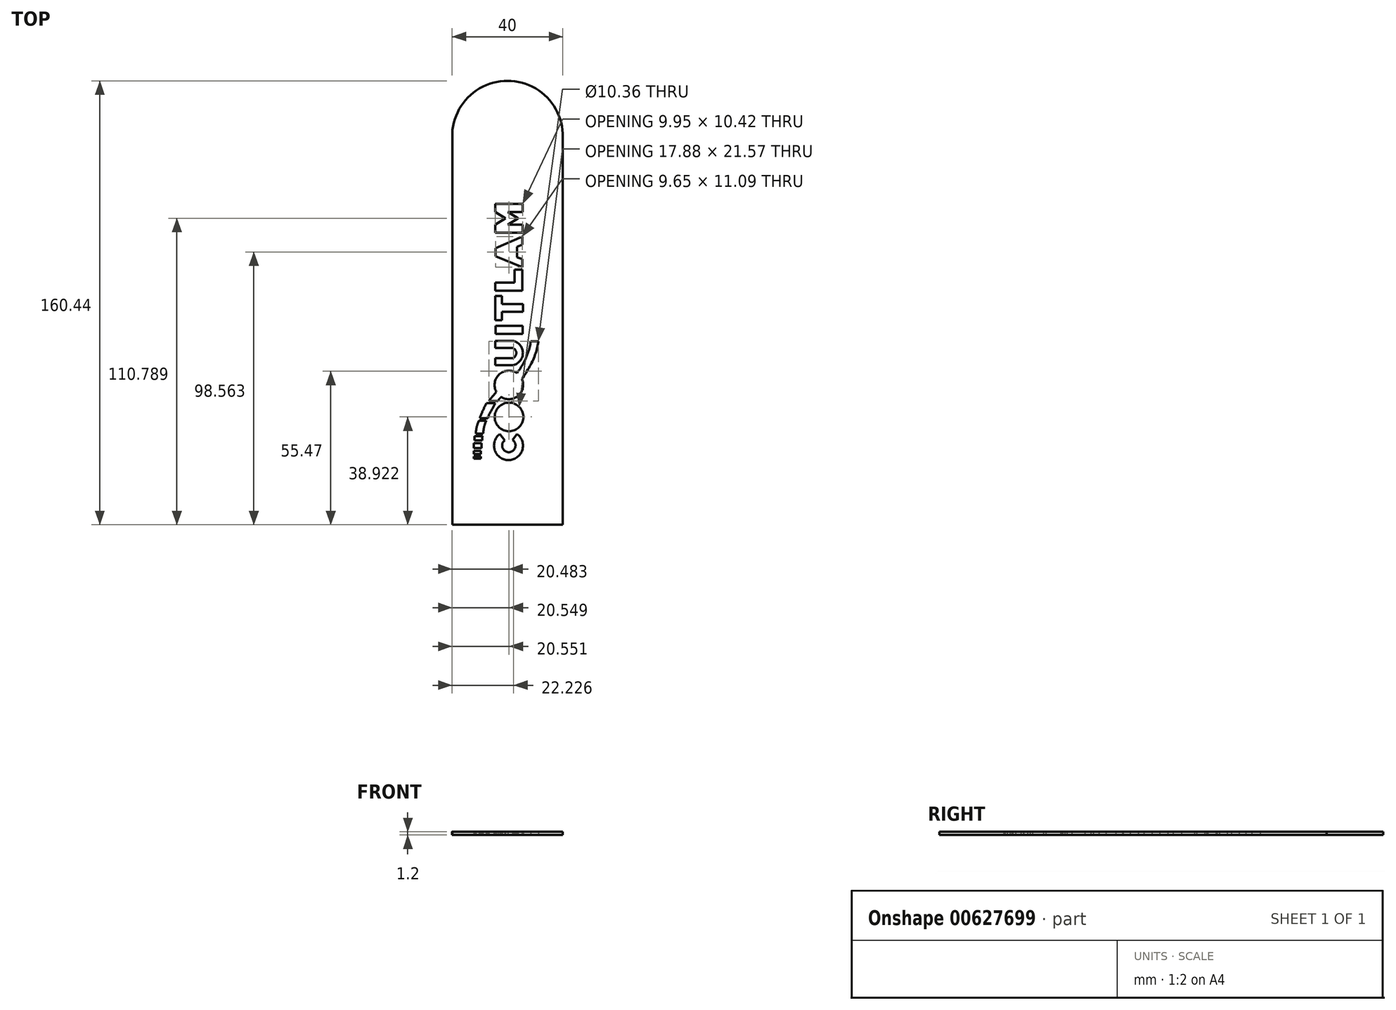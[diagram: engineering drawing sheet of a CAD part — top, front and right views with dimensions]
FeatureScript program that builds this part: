
annotation { "Feature Type Name" : "Feature", "Feature Type Description" : "" }
export const myFeature = defineFeature(function(context is Context, id is Id, definition is map)
    precondition{}
    {
        {
            var Q0;
            Q0=qCreatedBy(makeId("Top.planeOp"),FACE);
            var sketch = newSketch(context, id + "F0", { "sketchPlane" : qUnion([Q0])});
            skArc(sketch, "E0", {"start": v(-6.3, 54.09) * mm, "mid": v(-26.29, 74.53) * mm, "end": v(-46.28, 54.09) * mm});
            skLineSegment(sketch, "E1", {"start": v(-46.28, 54.09) * mm, "end": v(-46.28, -85.91) * mm});
            skLineSegment(sketch, "E2", {"start": v(-6.3, 54.09) * mm, "end": v(-6.3, -85.91) * mm});
            skLineSegment(sketch, "E3", {"start": v(-46.28, -85.91) * mm, "end": v(-6.3, -85.91) * mm});
            skArc(sketch, "E4", {"start": v(-27.3, -55.41) * mm, "mid": v(-25.75, -59.72) * mm, "end": v(-24.44, -55.33) * mm});
            skArc(sketch, "E5", {"start": v(-29.02, -53.12) * mm, "mid": v(-25.94, -62.57) * mm, "end": v(-22.87, -53.12) * mm});
            skLineSegment(sketch, "E6", {"start": v(-29.02, -53.12) * mm, "end": v(-27.3, -55.41) * mm});
            skLineSegment(sketch, "E7", {"start": v(-24.44, -55.33) * mm, "end": v(-22.87, -53.12) * mm});
            skCircle(sketch, "E8", {"center": v(-25.74, -46.99) * mm, "radius": 2.44 * mm});
            skCircle(sketch, "E9", {"center": v(-25.74, -46.99) * mm, "radius": 5.18 * mm});
            skLineSegment(sketch, "E10", {"start": v(-30.76, 1.6) * mm, "end": v(-30.76, -1.39) * mm});
            skLineSegment(sketch, "E11", {"start": v(-30.76, -1.39) * mm, "end": v(-20.98, -1.39) * mm});
            skLineSegment(sketch, "E12", {"start": v(-20.98, -1.39) * mm, "end": v(-20.98, 6.3) * mm});
            skLineSegment(sketch, "E13", {"start": v(-20.98, 6.3) * mm, "end": v(-23.72, 6.3) * mm});
            skLineSegment(sketch, "E14", {"start": v(-23.72, 6.3) * mm, "end": v(-23.72, 1.6) * mm});
            skLineSegment(sketch, "E15", {"start": v(-23.72, 1.6) * mm, "end": v(-30.76, 1.6) * mm});
            skLineSegment(sketch, "E16", {"start": v(-30.68, -3.24) * mm, "end": v(-30.68, -12) * mm});
            skLineSegment(sketch, "E17", {"start": v(-30.68, -12) * mm, "end": v(-28.35, -12) * mm});
            skLineSegment(sketch, "E18", {"start": v(-28.35, -12) * mm, "end": v(-28.35, -8.95) * mm});
            skLineSegment(sketch, "E19", {"start": v(-28.35, -8.95) * mm, "end": v(-20.76, -8.95) * mm});
            skLineSegment(sketch, "E20", {"start": v(-20.76, -8.95) * mm, "end": v(-20.76, -6.2) * mm});
            skLineSegment(sketch, "E21", {"start": v(-20.76, -6.2) * mm, "end": v(-28.35, -6.2) * mm});
            skLineSegment(sketch, "E22", {"start": v(-28.35, -6.2) * mm, "end": v(-28.35, -3.24) * mm});
            skLineSegment(sketch, "E23", {"start": v(-28.35, -3.24) * mm, "end": v(-30.68, -3.24) * mm});
            skArc(sketch, "E24", {"start": v(-24.25, -25.67) * mm, "mid": v(-23.12, -23.78) * mm, "end": v(-24.46, -22.03) * mm});
            skArc(sketch, "E25", {"start": v(-24.25, -28.22) * mm, "mid": v(-20.74, -23.75) * mm, "end": v(-24.46, -19.45) * mm});
            skLineSegment(sketch, "E26", {"start": v(-24.46, -19.45) * mm, "end": v(-30.73, -19.45) * mm});
            skLineSegment(sketch, "E27", {"start": v(-30.73, -19.45) * mm, "end": v(-30.73, -22.03) * mm});
            skLineSegment(sketch, "E28", {"start": v(-30.73, -22.03) * mm, "end": v(-24.46, -22.03) * mm});
            skLineSegment(sketch, "E29", {"start": v(-24.25, -25.67) * mm, "end": v(-30.73, -25.67) * mm});
            skLineSegment(sketch, "E30", {"start": v(-30.73, -25.67) * mm, "end": v(-30.73, -28.22) * mm});
            skLineSegment(sketch, "E31", {"start": v(-30.73, -28.22) * mm, "end": v(-24.25, -28.22) * mm});
            skLineSegment(sketch, "E32", {"start": v(-30.63, -13.98) * mm, "end": v(-30.63, -16.92) * mm});
            skLineSegment(sketch, "E33", {"start": v(-30.63, -16.92) * mm, "end": v(-20.8, -16.92) * mm});
            skLineSegment(sketch, "E34", {"start": v(-20.8, -16.92) * mm, "end": v(-20.8, -13.98) * mm});
            skLineSegment(sketch, "E35", {"start": v(-20.8, -13.98) * mm, "end": v(-30.63, -13.98) * mm});
            skLineSegment(sketch, "E36", {"start": v(-24.85, 13.76) * mm, "end": v(-24.85, 11.53) * mm});
            skLineSegment(sketch, "E37", {"start": v(-24.85, 11.53) * mm, "end": v(-27.5, 12.61) * mm});
            skLineSegment(sketch, "E38", {"start": v(-27.5, 12.61) * mm, "end": v(-24.85, 13.76) * mm});
            skLineSegment(sketch, "E39", {"start": v(-20.98, 18.2) * mm, "end": v(-30.63, 14.04) * mm});
            skLineSegment(sketch, "E40", {"start": v(-30.63, 14.04) * mm, "end": v(-30.63, 11.12) * mm});
            skLineSegment(sketch, "E41", {"start": v(-30.63, 11.12) * mm, "end": v(-20.98, 7.1) * mm});
            skLineSegment(sketch, "E42", {"start": v(-20.98, 7.1) * mm, "end": v(-20.98, 10.1) * mm});
            skLineSegment(sketch, "E43", {"start": v(-20.98, 10.1) * mm, "end": v(-22.8, 10.69) * mm});
            skLineSegment(sketch, "E44", {"start": v(-22.8, 10.69) * mm, "end": v(-22.8, 14.54) * mm});
            skLineSegment(sketch, "E45", {"start": v(-22.8, 14.54) * mm, "end": v(-20.98, 15.32) * mm});
            skLineSegment(sketch, "E46", {"start": v(-20.98, 15.32) * mm, "end": v(-20.98, 18.2) * mm});
            skLineSegment(sketch, "E47", {"start": v(-20.76, 19.67) * mm, "end": v(-30.72, 19.67) * mm});
            skLineSegment(sketch, "E48", {"start": v(-30.72, 19.67) * mm, "end": v(-30.72, 22.5) * mm});
            skLineSegment(sketch, "E49", {"start": v(-30.72, 22.5) * mm, "end": v(-27.1, 24.83) * mm});
            skLineSegment(sketch, "E50", {"start": v(-27.1, 24.83) * mm, "end": v(-30.72, 27.05) * mm});
            skLineSegment(sketch, "E51", {"start": v(-30.72, 27.05) * mm, "end": v(-30.72, 30.09) * mm});
            skLineSegment(sketch, "E52", {"start": v(-30.72, 30.09) * mm, "end": v(-20.76, 30.09) * mm});
            skLineSegment(sketch, "E53", {"start": v(-20.76, 30.09) * mm, "end": v(-20.76, 27.05) * mm});
            skLineSegment(sketch, "E54", {"start": v(-20.76, 27.05) * mm, "end": v(-26.15, 27.05) * mm});
            skLineSegment(sketch, "E55", {"start": v(-26.15, 27.05) * mm, "end": v(-22.52, 24.83) * mm});
            skLineSegment(sketch, "E56", {"start": v(-22.52, 24.83) * mm, "end": v(-26.15, 22.5) * mm});
            skLineSegment(sketch, "E57", {"start": v(-26.15, 22.5) * mm, "end": v(-20.76, 22.5) * mm});
            skLineSegment(sketch, "E58", {"start": v(-20.76, 22.5) * mm, "end": v(-20.76, 19.67) * mm});
            skLineSegment(sketch, "E59", {"start": v(-37.74, -53.07) * mm, "end": v(-35.16, -53.07) * mm});
            skLineSegment(sketch, "E60", {"start": v(-36.62, -48.28) * mm, "end": v(-33.96, -48.28) * mm});
            skFitSpline(sketch, "E61", {"points": [v(-33.96, -48.28) * mm, v(-35.16, -53.07) * mm], "startDerivative": vector(-2.34, -4.67) * mm, "endDerivative": vector(-0.73, -4.9) * mm});
            skLineSegment(sketch, "E62", {"start": v(-33.9, -42.04) * mm, "end": v(-30.66, -42.04) * mm});
            skLineSegment(sketch, "E63.bottom", {"start": v(-36.28, -47.39) * mm, "end": v(-33.39, -47.39) * mm});
            skLineSegment(sketch, "E63.top", {"start": v(-36.28, -47.39) * mm, "end": v(-33.39, -47.39) * mm});
            skLineSegment(sketch, "E63.left", {"start": v(-36.28, -47.39) * mm, "end": v(-36.28, -47.39) * mm});
            skLineSegment(sketch, "E63.right", {"start": v(-33.39, -47.39) * mm, "end": v(-33.39, -47.39) * mm});
            skFitSpline(sketch, "E64", {"points": [v(-33.9, -42.04) * mm, v(-36.28, -47.39) * mm], "startDerivative": vector(-2.85, -5.33) * mm, "endDerivative": vector(-1.75, -5.33) * mm});
            skFitSpline(sketch, "E65", {"points": [v(-30.66, -42.04) * mm, v(-33.39, -47.39) * mm], "startDerivative": vector(-3.36, -5.84) * mm, "endDerivative": vector(-1.75, -5.62) * mm});
            skLineSegment(sketch, "E66", {"start": v(-17.88, -19.65) * mm, "end": v(-15.13, -19.65) * mm});
            skFitSpline(sketch, "E67", {"points": [v(-15.13, -19.65) * mm, v(-21.13, -33.23) * mm], "startDerivative": vector(-1.76, -13.9) * mm, "endDerivative": vector(-9.3, -12.6) * mm});
            skFitSpline(sketch, "E68", {"points": [v(-17.88, -19.65) * mm, v(-22.88, -31.16) * mm], "startDerivative": vector(-1.76, -12.35) * mm, "endDerivative": vector(-7.81, -10.68) * mm});
            skCircle(sketch, "E69", {"center": v(-25.81, -35.4) * mm, "radius": 5.16 * mm});
            skLineSegment(sketch, "E70", {"start": v(-33, -41.23) * mm, "end": v(-29.76, -41.23) * mm});
            skFitSpline(sketch, "E71", {"points": [v(-30.31, -37.93) * mm, v(-33, -41.23) * mm], "startDerivative": vector(-3.27, -3.7) * mm, "endDerivative": vector(-1.73, -2.89) * mm});
            skFitSpline(sketch, "E72", {"points": [v(-28.57, -39.77) * mm, v(-29.76, -41.23) * mm], "startDerivative": vector(-1.34, -1.28) * mm, "endDerivative": vector(-0.7, -1.8) * mm});
            skArc(sketch, "E73", {"start": v(-26.63, -33.1) * mm, "mid": v(-27.84, -36.77) * mm, "end": v(-23.98, -37.02) * mm});
            skFitSpline(sketch, "E74", {"points": [v(-26.63, -33.1) * mm, v(-24.95, -33.1) * mm], "startDerivative": vector(1.68, 0) * mm, "endDerivative": vector(1.68, 0) * mm});
            skFitSpline(sketch, "E75", {"points": [v(-24.95, -33.1) * mm, v(-25.87, -34.22) * mm], "startDerivative": vector(-1.2, -1.19) * mm, "endDerivative": vector(-0.56, -1.4) * mm});
            skFitSpline(sketch, "E76", {"points": [v(-25.87, -34.22) * mm, v(-24.46, -36.33) * mm], "startDerivative": vector(1.42, -2.11) * mm, "endDerivative": vector(1.42, -2.11) * mm});
            skFitSpline(sketch, "E77", {"points": [v(-24.46, -36.33) * mm, v(-23.24, -35.34) * mm], "startDerivative": vector(1.57, 0.84) * mm, "endDerivative": vector(0.7, 1.34) * mm});
            skFitSpline(sketch, "E78", {"points": [v(-23.24, -35.34) * mm, v(-23.98, -37.02) * mm], "startDerivative": vector(0.33, -1.85) * mm, "endDerivative": vector(-1.27, -0.97) * mm});
            skFitSpline(sketch, "E79", {"points": [v(-36.62, -48.28) * mm, v(-37.74, -53.07) * mm], "startDerivative": vector(-2.08, -4.77) * mm, "endDerivative": vector(-0.06, -5.06) * mm});
            skLineSegment(sketch, "E80", {"start": v(-38.2, -55.46) * mm, "end": v(-38.2, -53.97) * mm});
            skLineSegment(sketch, "E81", {"start": v(-38.2, -53.97) * mm, "end": v(-35.3, -53.97) * mm});
            skLineSegment(sketch, "E82", {"start": v(-38.2, -55.46) * mm, "end": v(-35.48, -55.46) * mm});
            skFitSpline(sketch, "E83", {"points": [v(-35.3, -53.97) * mm, v(-35.48, -55.46) * mm], "startDerivative": vector(-0.36, -0.88) * mm, "endDerivative": vector(0, -1.45) * mm});
            skLineSegment(sketch, "E84.bottom", {"start": v(-38.44, -58.23) * mm, "end": v(-35.72, -58.23) * mm});
            skLineSegment(sketch, "E84.top", {"start": v(-38.44, -56.43) * mm, "end": v(-35.72, -56.43) * mm});
            skLineSegment(sketch, "E84.left", {"start": v(-38.44, -58.23) * mm, "end": v(-38.44, -56.43) * mm});
            skLineSegment(sketch, "E84.right", {"start": v(-35.72, -58.23) * mm, "end": v(-35.72, -56.43) * mm});
            skLineSegment(sketch, "E85", {"start": v(-38.5, -60.33) * mm, "end": v(-38.5, -59.27) * mm});
            skLineSegment(sketch, "E86", {"start": v(-38.5, -59.27) * mm, "end": v(-35.91, -59.27) * mm});
            skLineSegment(sketch, "E87", {"start": v(-35.91, -59.27) * mm, "end": v(-35.91, -60.33) * mm});
            skLineSegment(sketch, "E88", {"start": v(-35.91, -60.33) * mm, "end": v(-38.5, -60.33) * mm});
            skLineSegment(sketch, "E89", {"start": v(-38.5, -62.09) * mm, "end": v(-38.5, -61.3) * mm});
            skLineSegment(sketch, "E90", {"start": v(-38.5, -61.3) * mm, "end": v(-35.91, -61.3) * mm});
            skLineSegment(sketch, "E91", {"start": v(-35.91, -61.3) * mm, "end": v(-35.91, -62.09) * mm});
            skLineSegment(sketch, "E92", {"start": v(-35.91, -62.09) * mm, "end": v(-38.5, -62.09) * mm});
            skSolve(sketch);
        }
        {
            var Q0;
            Q0=makeQuery(id+"F0.imprint","IMPRINT",FACE,{"disambiguationData":[TD([[makeQuery(id+"F0.imprint","IMPRINT",EDGE,{"derivedFrom":sQuery(id+"F0.wireOp",EDGE,"E0")}),1.0]])]});
            extrude(context, id + "F1", {"entities" : qUnion([Q0]), "depth" : 1.2 * mm, "offsetDistance" : 25 * mm});
        }
    });
